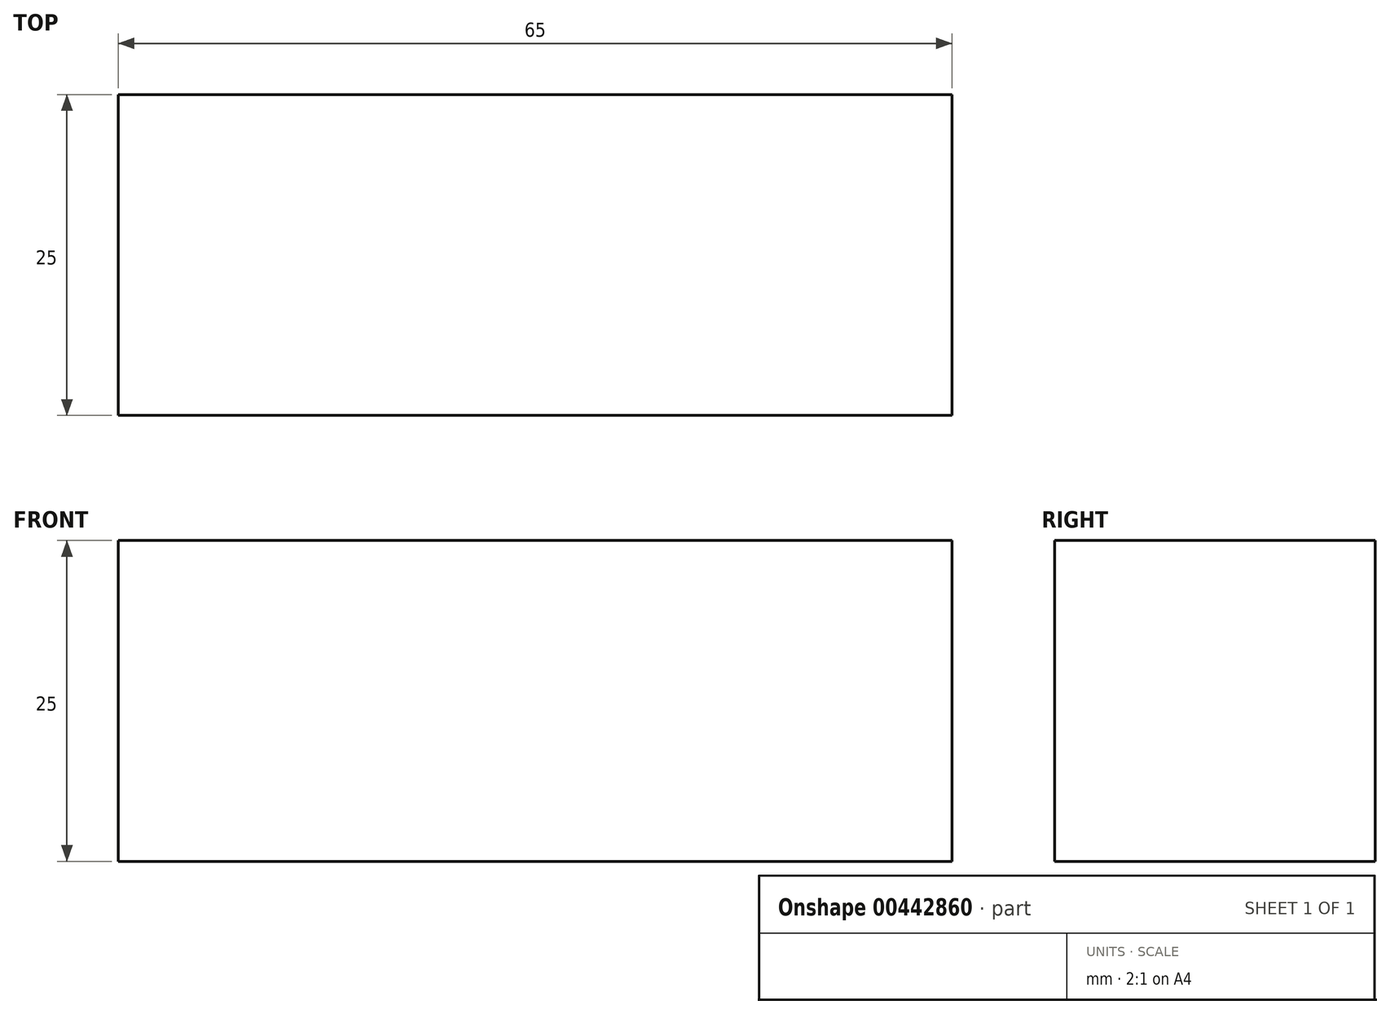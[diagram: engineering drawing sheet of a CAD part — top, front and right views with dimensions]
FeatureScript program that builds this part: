
annotation { "Feature Type Name" : "Feature", "Feature Type Description" : "" }
export const myFeature = defineFeature(function(context is Context, id is Id, definition is map)
    precondition{}
    {
        {
            var Q0;
            Q0=qCreatedBy(makeId("Front.planeOp"),FACE);
            var sketch = newSketch(context, id + "F0", { "sketchPlane" : qUnion([Q0])});
            skLineSegment(sketch, "E0", {"start": v(-32.5, 25) * mm, "end": v(-32.5, 0) * mm});
            skLineSegment(sketch, "E1", {"start": v(-32.5, 0) * mm, "end": v(32.5, 0) * mm});
            skLineSegment(sketch, "E2", {"start": v(32.5, 0) * mm, "end": v(32.5, 25) * mm});
            skLineSegment(sketch, "E3", {"start": v(-32.5, 25) * mm, "end": v(32.5, 25) * mm});
            skSolve(sketch);
        }
        {
            var Q0;
            Q0 = qSketchRegion(id + "F0", true);
            extrude(context, id + "F1", {"entities" : qUnion([Q0]), "depth" : 25 * mm});
        }
    });
